# Revit family: Haworth_EncloseFrameless_Door_SingleSwing
name_source: partatom
category: Furniture Systems
revit_build: Autodesk Revit 2018 (Build: 20170223_1515(x64)
units: mm (PartAtom-declared; Revit-internal decimal feet)

## family parameters
Always vertical = Yes
Cut with Voids When Loaded = No
OmniClass Number = 23.25.40.14
OmniClass Title = Demountable Partitions
Part Type = Normal
Room Calculation Point = No
Round Connector Dimension = Use Diameter
Shared = Yes
Work Plane-Based = No

## types (6) — shared parameters
Assembly Code = C1010200
Cap Height = 1 "
Ceiling Mount = Yes
Description = Door - Single Swing
Door Hardware Finish = Haworth _ Metal _ Brushed Aluminum
Door Pull Length = 16 "
Door Pull Offset = 1.66 "
Double Glazed = Yes
End of Run Finish = Haworth _ Polymer _ Black
End of Run Width = 0.155 "
Frame Depth = 4 "
Frame Finish = Haworth _ Metal _ Brushed Aluminum
Glass Depth = 0.4 "
Glass Finish = Haworth _ Glass _ Clear
Horizontal Frame Width = 0.875 "
Horizontal Top Adjuster Width = 2.625 "
Horizontal Top Trim Width = 1.5 "
Lever = No
Manufacturer = Haworth
Material Options = http://surfaces.haworth.com
Max. Height = 120 "
Max. Width = 48 "
Min. Height = 84 "
Min. Width = 24 "
Min/Max Height = 84-120 in.
Min/Max Width = 24-48 in.
Model = Haworth - Enclose Frameless
Pull Height Centerline = 40 "
Pull Offset Centerline = 2.755 "
Rectilinear D Pull = No
Revision Number = 3
Single Glazed = No
Size = Verify Final Dim. w/ Haworth
Sustainability Info = http://www.haworth.com
Tubular D Pull = Yes
URL = www.haworth.com
URL - Product = http://www.haworth.com
Vertical Frame Width = 0.875 "
Warranty = http://www.haworth.com

## per-type parameters (varying)
| type | Actual Door Height | Actual Door Width | Actual Height | Actual Width | Door Height | Door Leaf Width | Height | Width |
| 36" x 108" | 104.5 " | 33.94 " | 108 " | 36 " | 104.5 " | 33.94 " | 108 " | 36 " |
| 24" x 108" | 104.5 " | 21.94 " | 108 " | 24 " | 104.5 " | 21.94 " | 108 " | 24 " |
| 30" x 108" | 104.5 " | 27.94 " | 108 " | 30 " | 104.5 " | 27.94 " | 108 " | 30 " |
| 48" x 108" | 104.5 " | 45.94 " | 108 " | 48 " | 104.5 " | 45.94 " | 108 " | 48 " |
| 24" x 120" | 116.5 " | 21.94 " | 120 " | 24 " | 116.5 " | 21.94 " | 120 " | 24 " |
| 48" x 120" | 116.5 " | 45.94 " | 120 " | 48 " | 116.5 " | 45.94 " | 120 " | 48 " |

## geometry (parser evidence)
native form markers: Sweep x27
no freeform markers — native parametric forms only
